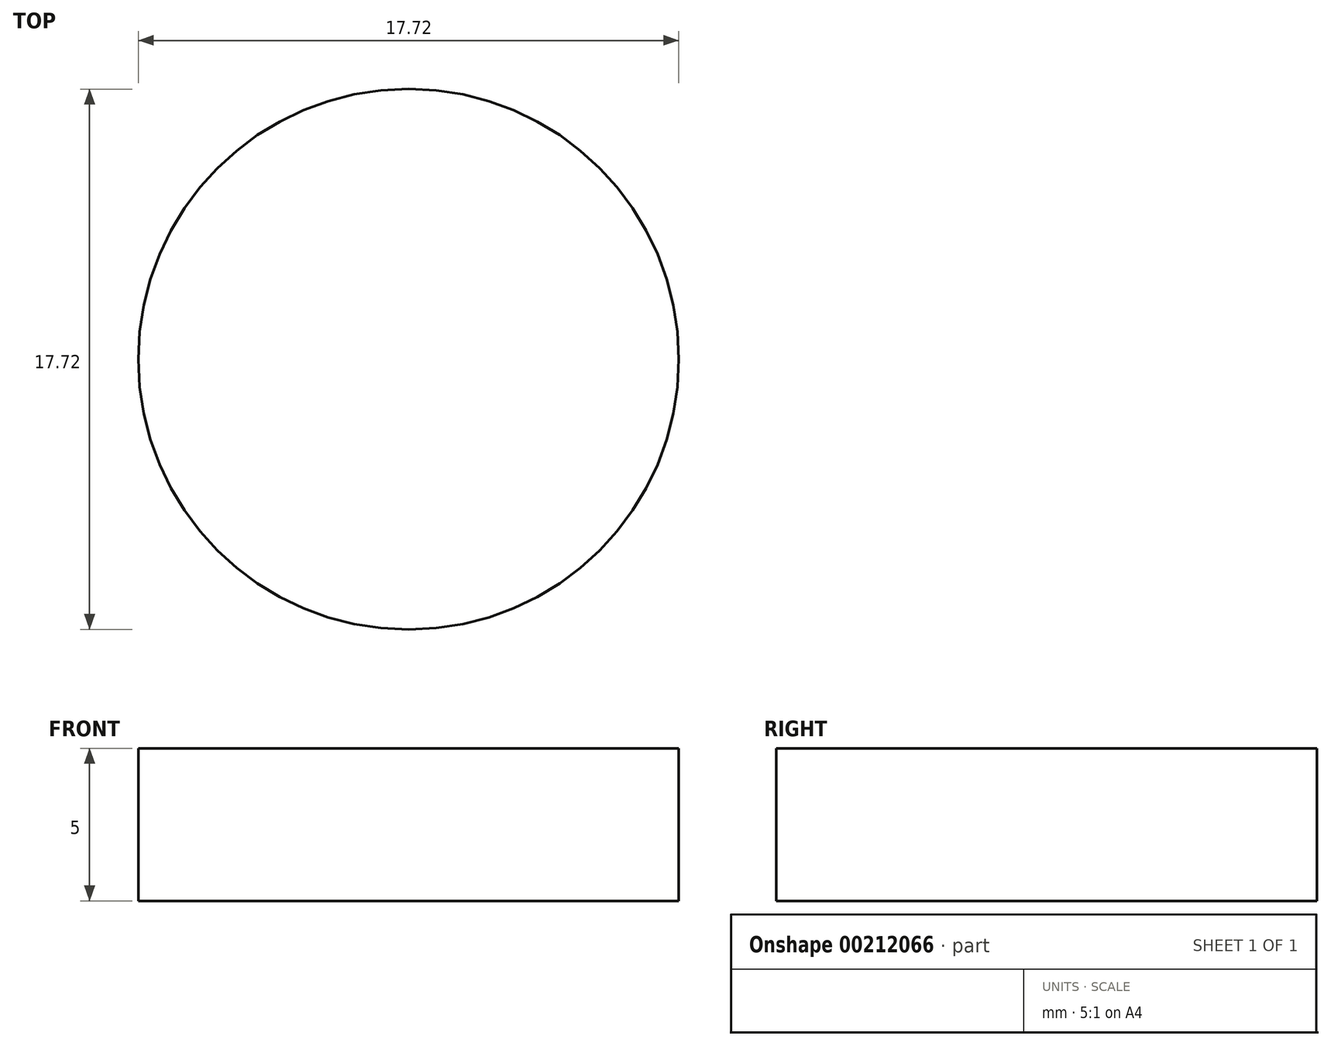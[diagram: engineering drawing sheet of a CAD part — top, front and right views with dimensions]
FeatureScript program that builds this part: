
annotation { "Feature Type Name" : "Feature", "Feature Type Description" : "" }
export const myFeature = defineFeature(function(context is Context, id is Id, definition is map)
    precondition{}
    {
        {
            var Q0;
            Q0=qCreatedBy(makeId("Top.planeOp"),FACE);
            var sketch = newSketch(context, id + "F0", { "sketchPlane" : qUnion([Q0])});
            skCircle(sketch, "E0", {"center": v(0, 0) * mm, "radius": 8.86 * mm});
            skSolve(sketch);
        }
        {
            var Q0;
            Q0=sQuery(id+"F0.wireOp",EDGE,"E0");
            extrude(context, id + "F1", {"bodyType" : ToolBodyType.SURFACE, "surfaceEntities" : qUnion([Q0]), "oppositeDirection" : true, "depth" : 5 * mm});
        }
    });
